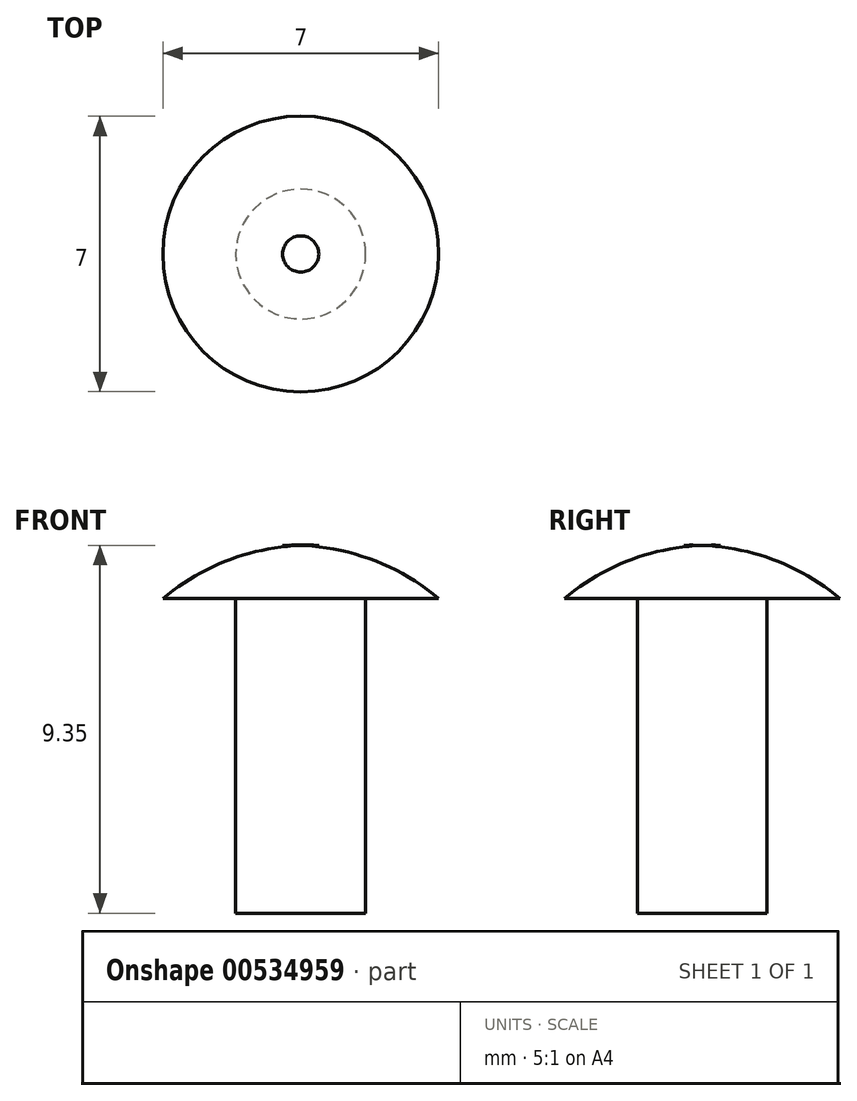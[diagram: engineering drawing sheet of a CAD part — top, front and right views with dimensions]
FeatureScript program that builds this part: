
annotation { "Feature Type Name" : "Feature", "Feature Type Description" : "" }
export const myFeature = defineFeature(function(context is Context, id is Id, definition is map)
    precondition{}
    {
        {
            var Q0;
            Q0=qCreatedBy(makeId("Top.planeOp"),FACE);
            var sketch = newSketch(context, id + "F0", { "sketchPlane" : qUnion([Q0])});
            skCircle(sketch, "E0", {"center": v(0, 0) * mm, "radius": 1.65 * mm});
            skSolve(sketch);
        }
        {
            var Q0;
            Q0 = qSketchRegion(id + "F0", true);
            extrude(context, id + "F1", {"entities" : qUnion([Q0]), "depth" : 8 * mm, "offsetDistance" : 25 * mm});
        }
        {
            var Q0;
            Q0=qCreatedBy(makeId("Right.planeOp"),FACE);
            var sketch = newSketch(context, id + "F2", { "sketchPlane" : qUnion([Q0])});
            skLineSegment(sketch, "E1", {"start": v(0, 8) * mm, "end": v(3.5, 8) * mm});
            skLineSegment(sketch, "E2", {"start": v(0, 8) * mm, "end": v(0, 9.35) * mm});
            skArc(sketch, "E3", {"start": v(3.5, 8) * mm, "mid": v(1.86, 8.96) * mm, "end": v(0, 9.35) * mm});
            skSolve(sketch);
        }
        {
            var Q0;
            Q0=makeQuery(id+"F2.imprint","IMPRINT",FACE,{"disambiguationData":[TD([[makeQuery(id+"F2.imprint","IMPRINT",EDGE,{"derivedFrom":sQuery(id+"F2.wireOp",EDGE,"E1")}),1.0]])]});
            var Q1;
            Q1=sQuery(id+"F2.wireOp",EDGE,"E2");
            revolve(context, id + "F3", {"operationType" : NewBodyOperationType.ADD, "entities" : qUnion([Q0]), "axis" : qUnion([Q1]), "revolveType" : RevolveType.FULL});
        }
    });
